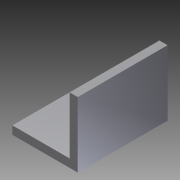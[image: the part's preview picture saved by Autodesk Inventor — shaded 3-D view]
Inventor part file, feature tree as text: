
AUTODESK INVENTOR PART (.ipt)
format: ipt  version: 2012 (Build 160160000, 160)  size: 74,240 bytes
history: native  units: in
note: dims shown in document units (in); Inventor stores cm internally (conversion verified against a paired STEP export)
features: extrude x1, sketch x1
ambient origin geometry x8: Origin, YZ Plane, XZ Plane, XY Plane, X Axis, Y Axis, Z Axis, Center Point
bodies: Solid1 (feature_tree)
feature tree (2):
  extrude  "Extrusion1"  Depth=0.125in
  sketch  "Sketch1"  dims[d0=0.125in d1=0.125in d2=1.0in d3=1.0in d4=1.375in d5=0.0in]
